# Revit family: 2100.112 Rainhead Overflow Sump 530x380x240
name_source: partatom
category: Plumbing Fixtures
revit_build: Autodesk Revit 2016 (Build: 20150714_1515(x64)
units: mm (PartAtom-declared; Revit-internal decimal feet)

## family parameters
Always vertical = No
Cut with Voids When Loaded = No
OmniClass Number = 23.60.30.11
OmniClass Title = Pipework Products for General Use
Part Type = Normal
Room Calculation Point = No
Round Connector Dimension = Use Diameter
Shared = No
Work Plane-Based = No

## types (2) — shared parameters
CW Connection = No
Connector Description = DWV100
CutOut Length = 395 mm  [stored 1.29593 ft]
CutOut Width = 245 mm  [stored 0.803806 ft]
DVW150 Nozzle Heigth = 264 mm  [stored 0.866142 ft]
DWV100 Nozzle Height = 329 mm  [stored 1.0794 ft]
Flow = 0.0 L/s
HW Connection = No
Left Edge Position = 170 mm  [stored 0.557743 ft]
Left Edge Void Position = 167 mm  [stored 0.5479 ft]
Length = 528 mm
Manufacturer = Aquanight Industries Ltd
Material = Aquanight-Black
Model = 2100.112
Nozzles Distance = 185 mm  [stored 0.606955 ft]
Pool Depth = 204 mm
Right Edge Position = 83 mm
Right Edge Void Position = 80 mm
URL = www.aquaknight.co.nz
Vent Connection = No
Waste Connection = Yes
Width = 378 mm  [stored 1.24016 ft]
zero-valued in all types: Left Tube End

## per-type parameters (varying)
| type | Connector Diameter | Connector Location | Description |
| DWV100 | 100 mm  [stored 0.328084 ft] | 297 mm | Membrane Rainhead 530x380x330 DWV100 DN100 |
| DWV150 | 150 mm | 234 mm  [stored 0.767717 ft] | Membrane Rainhead 530x380x330 DWV150 DN150 |

note: [stored X ft] marks values corroborated as IEEE doubles in the binary element streams (Revit-internal decimal feet)

## geometry (parser evidence)
native form markers: Sweep x2
no freeform markers — native parametric forms only
